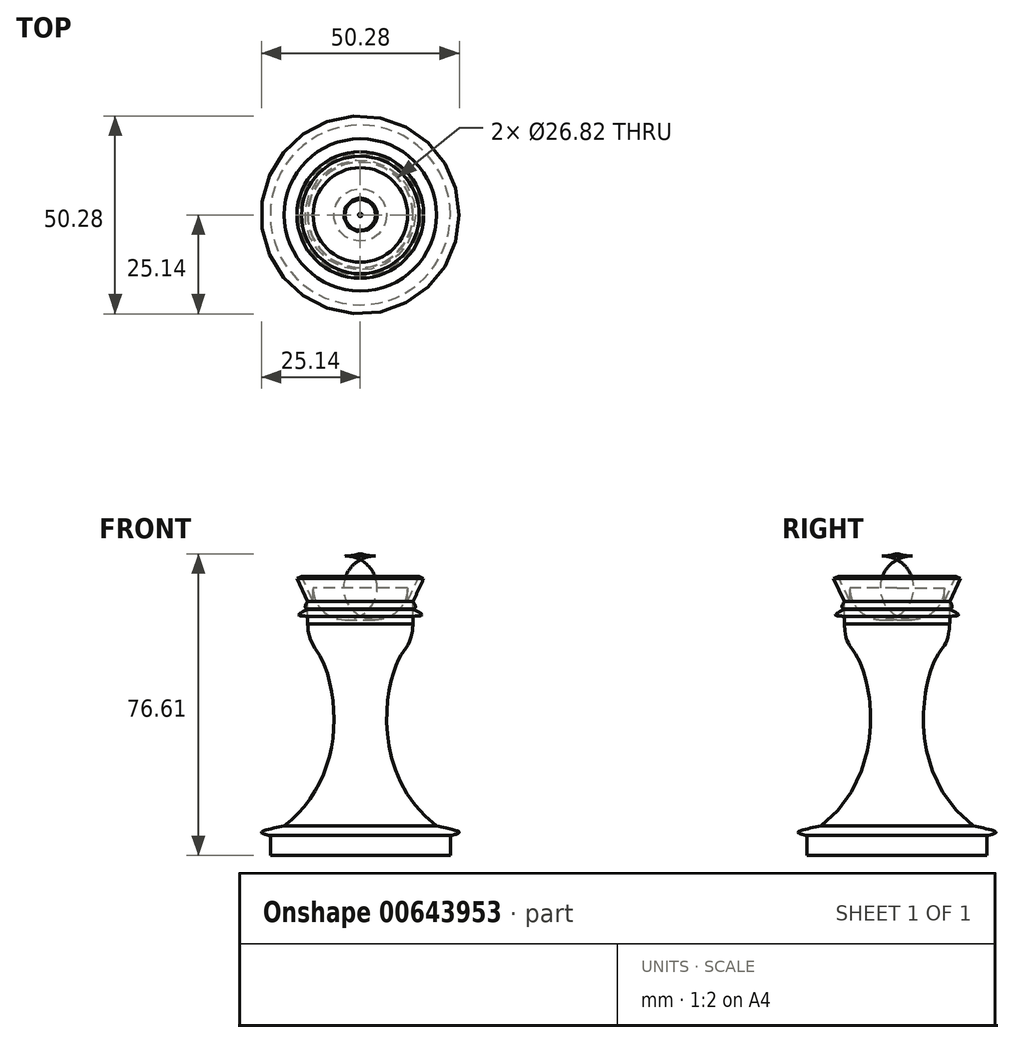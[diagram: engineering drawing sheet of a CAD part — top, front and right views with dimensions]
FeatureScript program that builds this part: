
annotation { "Feature Type Name" : "Feature", "Feature Type Description" : "" }
export const myFeature = defineFeature(function(context is Context, id is Id, definition is map)
    precondition{}
    {
        {
            var Q0;
            Q0=qCreatedBy(makeId("Front.planeOp"),FACE);
            var sketch = newSketch(context, id + "F0", { "sketchPlane" : qUnion([Q0])});
            skLineSegment(sketch, "E0", {"start": v(0, 0) * mm, "end": v(22.86, 0) * mm});
            skLineSegment(sketch, "E1", {"start": v(0, 74.76) * mm, "end": v(0, 55.71) * mm});
            skLineSegment(sketch, "E2", {"start": v(0, 55.71) * mm, "end": v(13.4, 55.71) * mm});
            skLineSegment(sketch, "E3", {"start": v(0, 55.71) * mm, "end": v(0, 0) * mm});
            skFitSpline(sketch, "E4", {"points": [v(22.86, 0) * mm, v(9.85, 45) * mm, v(13.4, 55.71) * mm], "startDerivative": vector(-94.74, 57.84) * mm, "endDerivative": vector(-0.02, 70.67) * mm});
            skLineSegment(sketch, "E5", {"start": v(22.86, 0) * mm, "end": v(22.86, -5.08) * mm});
            skLineSegment(sketch, "E6", {"start": v(22.86, -5.08) * mm, "end": v(0, -5.08) * mm});
            skLineSegment(sketch, "E7", {"start": v(0, -5.08) * mm, "end": v(0, 0) * mm});
            skLineSegment(sketch, "E8", {"start": v(13.4, 55.71) * mm, "end": v(13.4, 59.52) * mm});
            skLineSegment(sketch, "E9", {"start": v(13.4, 59.52) * mm, "end": v(0, 59.52) * mm});
            skLineSegment(sketch, "E10", {"start": v(13.4, 59.52) * mm, "end": v(31.84, 59.52) * mm, "construction": true});
            skLineSegment(sketch, "E11", {"start": v(13.4, 59.52) * mm, "end": v(16.1, 65.28) * mm});
            skLineSegment(sketch, "E12", {"start": v(10.55, 59.46) * mm, "end": v(10.55, 62) * mm, "construction": true});
            skLineSegment(sketch, "E13", {"start": v(16.1, 65.28) * mm, "end": v(14.94, 65.81) * mm});
            skLineSegment(sketch, "E14", {"start": v(14.94, 65.81) * mm, "end": v(12, 59.52) * mm});
            skLineSegment(sketch, "E15", {"start": v(12, 59.52) * mm, "end": v(12, 71.04) * mm});
            skLineSegment(sketch, "E16", {"start": v(12, 71.04) * mm, "end": v(0, 71.04) * mm});
            skLineSegment(sketch, "E17", {"start": v(0.43, 71.04) * mm, "end": v(0.43, 71.53) * mm});
            skArc(sketch, "E18", {"start": v(0.43, 71.53) * mm, "mid": v(1.1, 72.66) * mm, "end": v(0, 73.39) * mm});
            skArc(sketch, "E19", {"start": v(13.37, 53.77) * mm, "mid": v(14.38, 54.72) * mm, "end": v(13.4, 55.71) * mm});
            skFitSpline(sketch, "E20", {"points": [v(13.37, 53.77) * mm, v(15.64, 53.46) * mm, v(13.22, 51.96) * mm], "startDerivative": vector(7.01, -0.16) * mm, "endDerivative": vector(-7.06, -3.42) * mm});
            skLineSegment(sketch, "E21", {"start": v(13.4, 54.74) * mm, "end": v(14.38, 54.74) * mm, "construction": true});
            skFitSpline(sketch, "E22.MirrorCS", {"points": [v(13.37, 55.7) * mm, v(15.64, 56.03) * mm, v(13.22, 57.53) * mm], "startDerivative": vector(7.01, 0.16) * mm, "endDerivative": vector(-7.06, 3.42) * mm});
            skPoint(sketch, "E23.2.internal.snap0", {"position": v(13.4, 57.62) * mm});
            skFitSpline(sketch, "E23", {"points": [v(13.4, 59.52) * mm, v(13.98, 57.98) * mm, v(13.4, 57.53) * mm], "startDerivative": vector(1.66, -3) * mm, "endDerivative": vector(-1.9, -0.85) * mm});
            skFitSpline(sketch, "E24", {"points": [v(22.86, 0) * mm, v(25.14, 0.8) * mm, v(19.34, 2.43) * mm], "startDerivative": vector(8.84, 1.91) * mm, "endDerivative": vector(-14.13, 2.9) * mm});
            skSolve(sketch);
        }
        {
            var Q0;
            {var subQ0=sQuery(id+"F0.wireOp",EDGE,"E11");Q0=makeQuery(id+"F0.imprint","IMPRINT",FACE,{"disambiguationData":[TD([[makeQuery(id+"F0.imprint","IMPRINT",EDGE,{"derivedFrom":subQ0}),1.0]])]});}
            var Q1;
            {var subQ0=sQuery(id+"F0.wireOp",EDGE,"E9");var subQ1=sQuery(id+"F0.wireOp",EDGE,"E1");var subQ2=makeQuery(id+"F0.imprint","INTERSECT",VERTEX,{"derivedFrom":[subQ1,subQ0]});Q1=makeQuery(id+"F0.imprint","IMPRINT",FACE,{"disambiguationData":[TD([[makeQuery(id+"F0.imprint","IMPRINT",EDGE,{"disambiguationData":[TD([[subQ2,1.0]])],"derivedFrom":subQ1}),1.0]])]});}
            var Q2;
            {var subQ3=sQuery(id+"F0.wireOp",EDGE,"E2");Q2=makeQuery(id+"F0.imprint","IMPRINT",FACE,{"disambiguationData":[TD([[makeQuery(id+"F0.imprint","IMPRINT",EDGE,{"derivedFrom":subQ3}),1.0]])]});}
            var Q3;
            Q3=makeQuery(id+"F0.imprint","IMPRINT",FACE,{"disambiguationData":[TD([[makeQuery(id+"F0.imprint","IMPRINT",EDGE,{"derivedFrom":sQuery(id+"F0.wireOp",EDGE,"E0")}),-1.0]])]});
            var Q4;
            Q4=makeQuery(id+"F0.imprint","IMPRINT",FACE,{"disambiguationData":[TD([[makeQuery(id+"F0.imprint","IMPRINT",EDGE,{"derivedFrom":sQuery(id+"F0.wireOp",EDGE,"E0")}),1.0]])]});
            var Q5;
            {var subQ4=sQuery(id+"F0.wireOp",EDGE,"E17");Q5=makeQuery(id+"F0.imprint","IMPRINT",FACE,{"disambiguationData":[TD([[makeQuery(id+"F0.imprint","IMPRINT",EDGE,{"derivedFrom":subQ4}),1.0]])]});}
            var Q6;
            {var subQ0=sQuery(id+"F0.wireOp",EDGE,"E20");var subQ1=sQuery(id+"F0.wireOp",EDGE,"E4");var subQ2=makeQuery(id+"F0.imprint","INTERSECT",VERTEX,{"disambiguationData":[OD(0.0)],"derivedFrom":[subQ1,subQ0]});Q6=makeQuery(id+"F0.imprint","IMPRINT",FACE,{"disambiguationData":[TD([[makeQuery(id+"F0.imprint","IMPRINT",EDGE,{"disambiguationData":[TD([[subQ2,1.0]])],"derivedFrom":subQ1}),-1.0]])]});}
            var Q7;
            {var subQ0=sQuery(id+"F0.wireOp",EDGE,"E19");Q7=makeQuery(id+"F0.imprint","IMPRINT",FACE,{"disambiguationData":[TD([[makeQuery(id+"F0.imprint","IMPRINT",EDGE,{"derivedFrom":subQ0}),1.0]])]});}
            var Q8;
            {var subQ0=sQuery(id+"F0.wireOp",EDGE,"E22.MirrorCS");var subQ1=sQuery(id+"F0.wireOp",EDGE,"E8");var subQ3=makeQuery(id+"F0.imprint","INTERSECT",VERTEX,{"derivedFrom":[subQ1,subQ0]});Q8=makeQuery(id+"F0.imprint","IMPRINT",FACE,{"disambiguationData":[TD([[makeQuery(id+"F0.imprint","IMPRINT",EDGE,{"disambiguationData":[TD([[subQ3,1.0]])],"derivedFrom":subQ1}),-1.0]])]});}
            var Q9;
            {var subQ0=sQuery(id+"F0.wireOp",EDGE,"E23");Q9=makeQuery(id+"F0.imprint","IMPRINT",FACE,{"disambiguationData":[TD([[makeQuery(id+"F0.imprint","IMPRINT",EDGE,{"derivedFrom":subQ0}),-1.0]])]});}
            var Q10;
            {var subQ0=sQuery(id+"F0.wireOp",EDGE,"E24");Q10=makeQuery(id+"F0.imprint","IMPRINT",FACE,{"disambiguationData":[TD([[makeQuery(id+"F0.imprint","IMPRINT",EDGE,{"derivedFrom":subQ0}),1.0]])]});}
            var Q11;
            Q11=sQuery(id+"F0.wireOp",EDGE,"E1");
            revolve(context, id + "F1", {"entities" : qUnion([Q0, Q1, Q2, Q3, Q4, Q5, Q6, Q7, Q8, Q9, Q10]), "axis" : qUnion([Q11]), "revolveType" : RevolveType.FULL});
        }
        {
            var Q0;
            Q0=makeQuery(id+"F1.opRevolve","SWEPT_FACE",FACE,{"disambiguationData":[OSD([sQuery(id+"F0.wireOp",EDGE,"E16")])]});
            fillet(context, id + "F2", {"entities" : qUnion([Q0]), "radius" : 8.13 * mm, "tangentPropagation" : true, "allowEdgeOverflow" : false});
        }
    });
